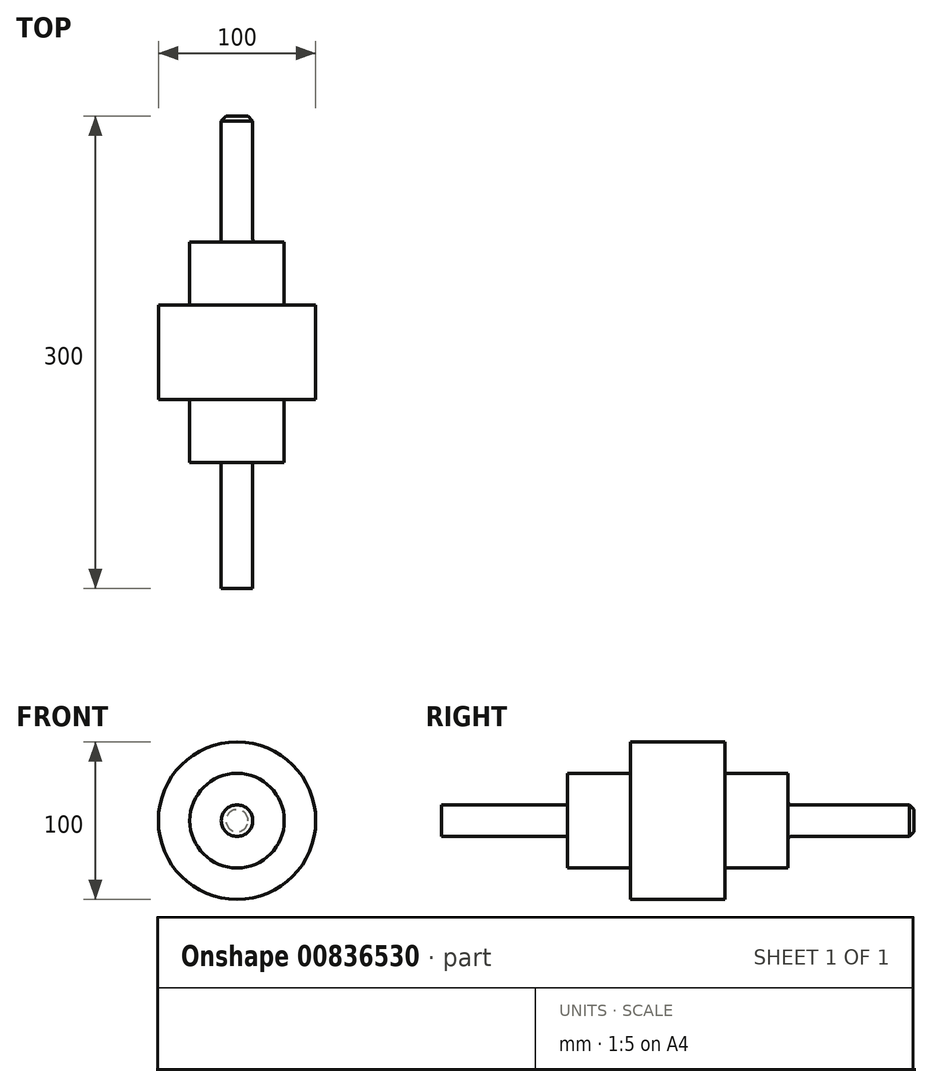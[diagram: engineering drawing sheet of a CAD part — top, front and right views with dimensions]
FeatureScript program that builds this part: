
annotation { "Feature Type Name" : "Feature", "Feature Type Description" : "" }
export const myFeature = defineFeature(function(context is Context, id is Id, definition is map)
    precondition{}
    {
        {
            var Q0;
            Q0=qCreatedBy(makeId("Top.planeOp"),FACE);
            var sketch = newSketch(context, id + "F0", { "sketchPlane" : qUnion([Q0])});
            skLineSegment(sketch, "E0", {"start": v(10, 55.72) * mm, "end": v(30, 55.72) * mm});
            skLineSegment(sketch, "E1", {"start": v(30, 55.72) * mm, "end": v(30, 15.72) * mm});
            skLineSegment(sketch, "E2", {"start": v(30, 15.72) * mm, "end": v(50, 15.72) * mm});
            skLineSegment(sketch, "E3", {"start": v(50, 15.72) * mm, "end": v(50, -44.28) * mm});
            skLineSegment(sketch, "E4", {"start": v(50, -44.28) * mm, "end": v(30, -44.28) * mm});
            skLineSegment(sketch, "E5", {"start": v(30, -44.28) * mm, "end": v(30, -84.28) * mm});
            skLineSegment(sketch, "E6", {"start": v(30, -84.28) * mm, "end": v(10, -84.28) * mm});
            skLineSegment(sketch, "E7", {"start": v(10, -84.28) * mm, "end": v(10, -164.28) * mm});
            skLineSegment(sketch, "E8", {"start": v(10, -164.28) * mm, "end": v(0, -164.28) * mm});
            skLineSegment(sketch, "E9", {"start": v(10, 55.72) * mm, "end": v(10, 135.72) * mm});
            skLineSegment(sketch, "E10", {"start": v(10, 135.72) * mm, "end": v(0, 135.72) * mm});
            skLineSegment(sketch, "E11", {"start": v(0, 135.72) * mm, "end": v(0, -164.28) * mm});
            skSolve(sketch);
        }
        {
            var Q0;
            Q0 = qSketchRegion(id + "F0", true);
            var Q1;
            Q1=sQuery(id+"F0.wireOp",EDGE,"E11");
            revolve(context, id + "F1", {"surfaceOperationType" : NewSurfaceOperationType.NEW, "entities" : qUnion([Q0]), "axis" : qUnion([Q1]), "revolveType" : RevolveType.FULL});
        }
        {
            var Q0;
            Q0=makeQuery(id+"F1.opRevolve","SWEPT_EDGE",EDGE,{"disambiguationData":[OSD([sQuery(id+"F0.wireOp",EDGE,"E0"),sQuery(id+"F0.wireOp",EDGE,"E9")])]});
            fillet(context, id + "F2", {"entities" : qUnion([Q0]), "radius" : 2 * mm, "tangentPropagation" : true, "defaultsChanged" : false, "allowEdgeOverflow" : false, "vertexSettings" : [], "filletType" : FilletType.EDGE});
        }
        {
            var Q0;
            Q0=makeQuery(id+"F1.opRevolve","SWEPT_EDGE",EDGE,{"disambiguationData":[OSD([sQuery(id+"F0.wireOp",EDGE,"E9"),sQuery(id+"F0.wireOp",EDGE,"E10")])]});
            chamfer(context, id + "F3", {"entities" : qUnion([Q0]), "width" : 3 * mm, "tangentPropagation" : true});
        }
    });
